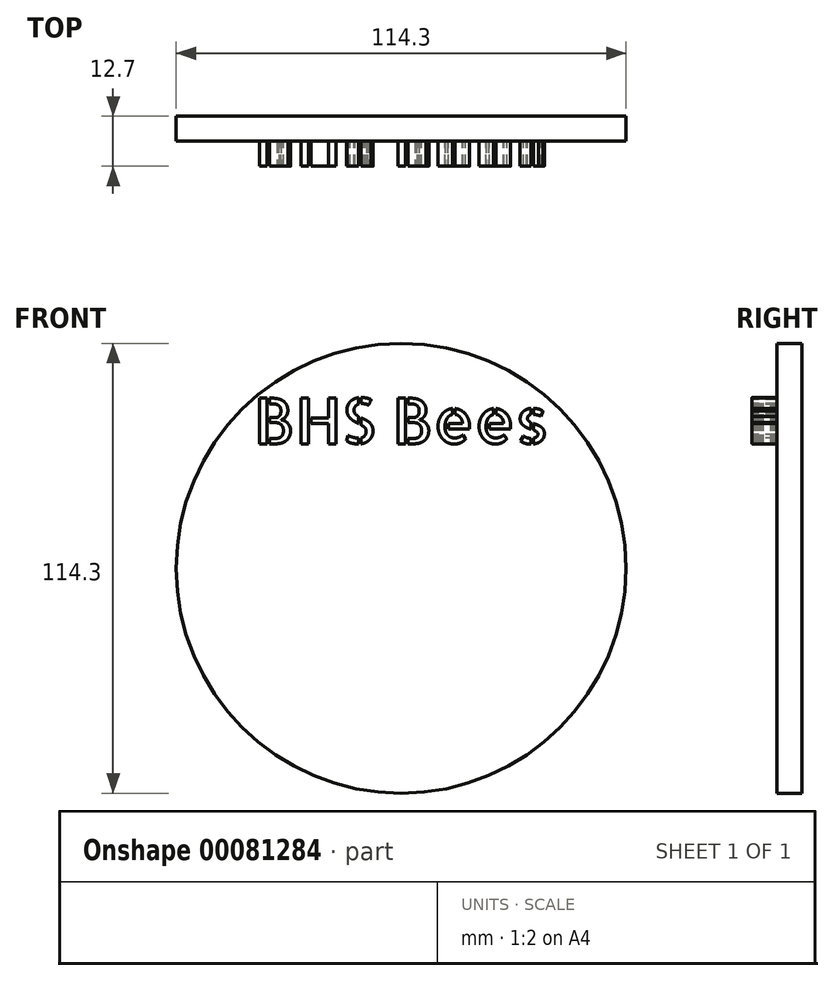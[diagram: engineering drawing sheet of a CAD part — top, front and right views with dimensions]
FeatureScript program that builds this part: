
annotation { "Feature Type Name" : "Feature", "Feature Type Description" : "" }
export const myFeature = defineFeature(function(context is Context, id is Id, definition is map)
    precondition{}
    {
        {
            var Q0;
            Q0=qCreatedBy(makeId("Front.planeOp"),FACE);
            var sketch = newSketch(context, id + "F0", { "sketchPlane" : qUnion([Q0])});
            skCircle(sketch, "E0", {"center": v(0, 0) * mm, "radius": 57.15 * mm});
            skSolve(sketch);
        }
        {
            var Q0;
            Q0 = qSketchRegion(id + "F0", true);
            extrude(context, id + "F1", {"entities" : qUnion([Q0]), "depth" : 6.35 * mm});
        }
        {
            var Q0;
            Q0=makeQuery(id+"F1.opExtrude","CAP_FACE",FACE,{"disambiguationData":[OSD([sQuery(id+"F0.wireOp",EDGE,"E0")])],"isStart":false});
            var sketch = newSketch(context, id + "F2", { "sketchPlane" : qUnion([Q0])});
            skText(sketch, "E1", { "text": "BHS Bees", "fontName": "AllertaStencil-Regular.ttf"});
            const initialGuessF2  = {"E1": [-0.03743, 0.03164, 1, 0, 0.01158]};
            skSetInitialGuess(sketch, initialGuessF2);
            skSolve(sketch);
        }
        {
            var Q0;
            Q0 = qSketchRegion(id + "F2", true);
            extrude(context, id + "F3", {"entities" : qUnion([Q0]), "operationType" : NewBodyOperationType.ADD, "depth" : 6.35 * mm});
        }
    });
